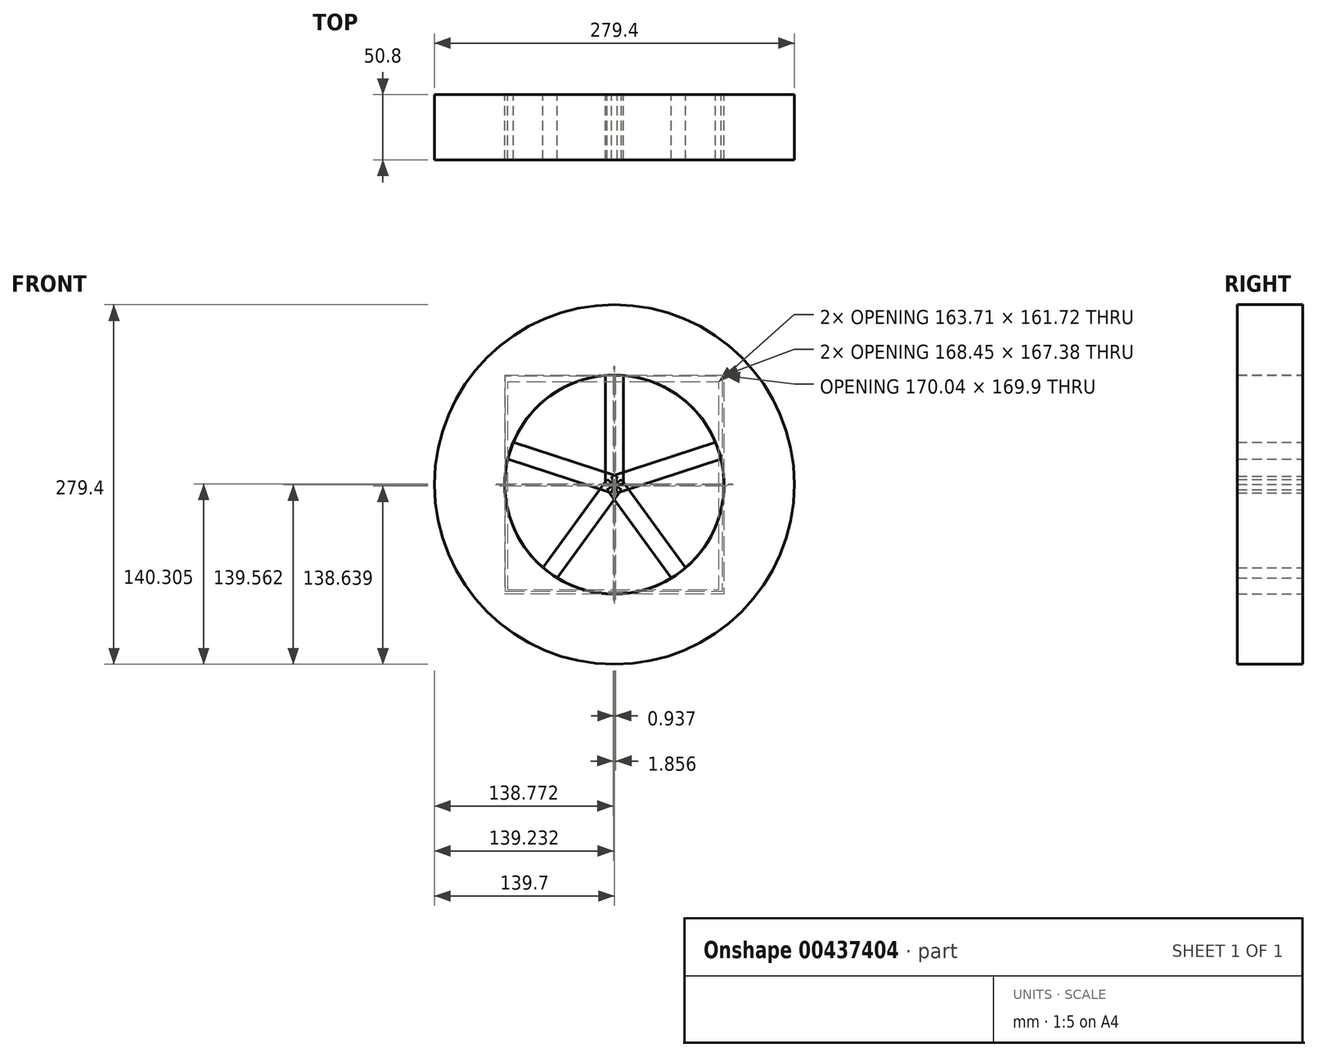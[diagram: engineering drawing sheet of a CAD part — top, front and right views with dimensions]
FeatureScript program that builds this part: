
annotation { "Feature Type Name" : "Feature", "Feature Type Description" : "" }
export const myFeature = defineFeature(function(context is Context, id is Id, definition is map)
    precondition{}
    {
        {
            var Q0;
            Q0=qCreatedBy(makeId("Front.planeOp"),FACE);
            var sketch = newSketch(context, id + "F0", { "sketchPlane" : qUnion([Q0])});
            skCircle(sketch, "E0", {"center": v(0, 0) * mm, "radius": 139.7 * mm});
            skCircle(sketch, "E1", {"center": v(0, 0) * mm, "radius": 85.1 * mm});
            skSolve(sketch);
        }
        {
            var Q0;
            Q0 = qSketchRegion(id + "F0", true);
            extrude(context, id + "F1", {"entities" : qUnion([Q0]), "endBound" : BoundingType.SYMMETRIC, "depth" : 50.8 * mm});
        }
        {
            var Q0;
            Q0=qCreatedBy(makeId("Front.planeOp"),FACE);
            var sketch = newSketch(context, id + "F2", { "sketchPlane" : qUnion([Q0])});
            skLineSegment(sketch, "E2.bottom", {"start": v(-6.86, 101.6) * mm, "end": v(6.86, 101.6) * mm});
            skLineSegment(sketch, "E2.top", {"start": v(-6.86, 0) * mm, "end": v(6.86, 0) * mm});
            skLineSegment(sketch, "E2.left", {"start": v(-6.86, 101.6) * mm, "end": v(-6.86, 0) * mm});
            skLineSegment(sketch, "E2.right", {"start": v(6.86, 101.6) * mm, "end": v(6.86, 0) * mm});
            skSolve(sketch);
        }
        {
            var Q0;
            Q0 = qSketchRegion(id + "F2", true);
            extrude(context, id + "F3", {"entities" : qUnion([Q0]), "operationType" : NewBodyOperationType.ADD, "endBound" : BoundingType.SYMMETRIC, "depth" : 50.8 * mm});
        }
        {
            var Q0;
            Q0=makeQuery(id+"F1.opExtrude","SWEPT_BODY",BODY,{"disambiguationData":[OSD([sQuery(id+"F0.wireOp",EDGE,"E0"),sQuery(id+"F0.wireOp",EDGE,"E1")])]});
            var Q1;
            Q1=makeQuery(id+"F1.opExtrude","SWEPT_FACE",FACE,{"disambiguationData":[OSD([sQuery(id+"F0.wireOp",EDGE,"E0")])]});
            circularPattern(context, id + "F4", {"entities" : qUnion([Q0]), "axis" : qUnion([Q1]), "angle" : 360 * degree, "instanceCount" : 5, "equalSpace" : true});
        }
    });
